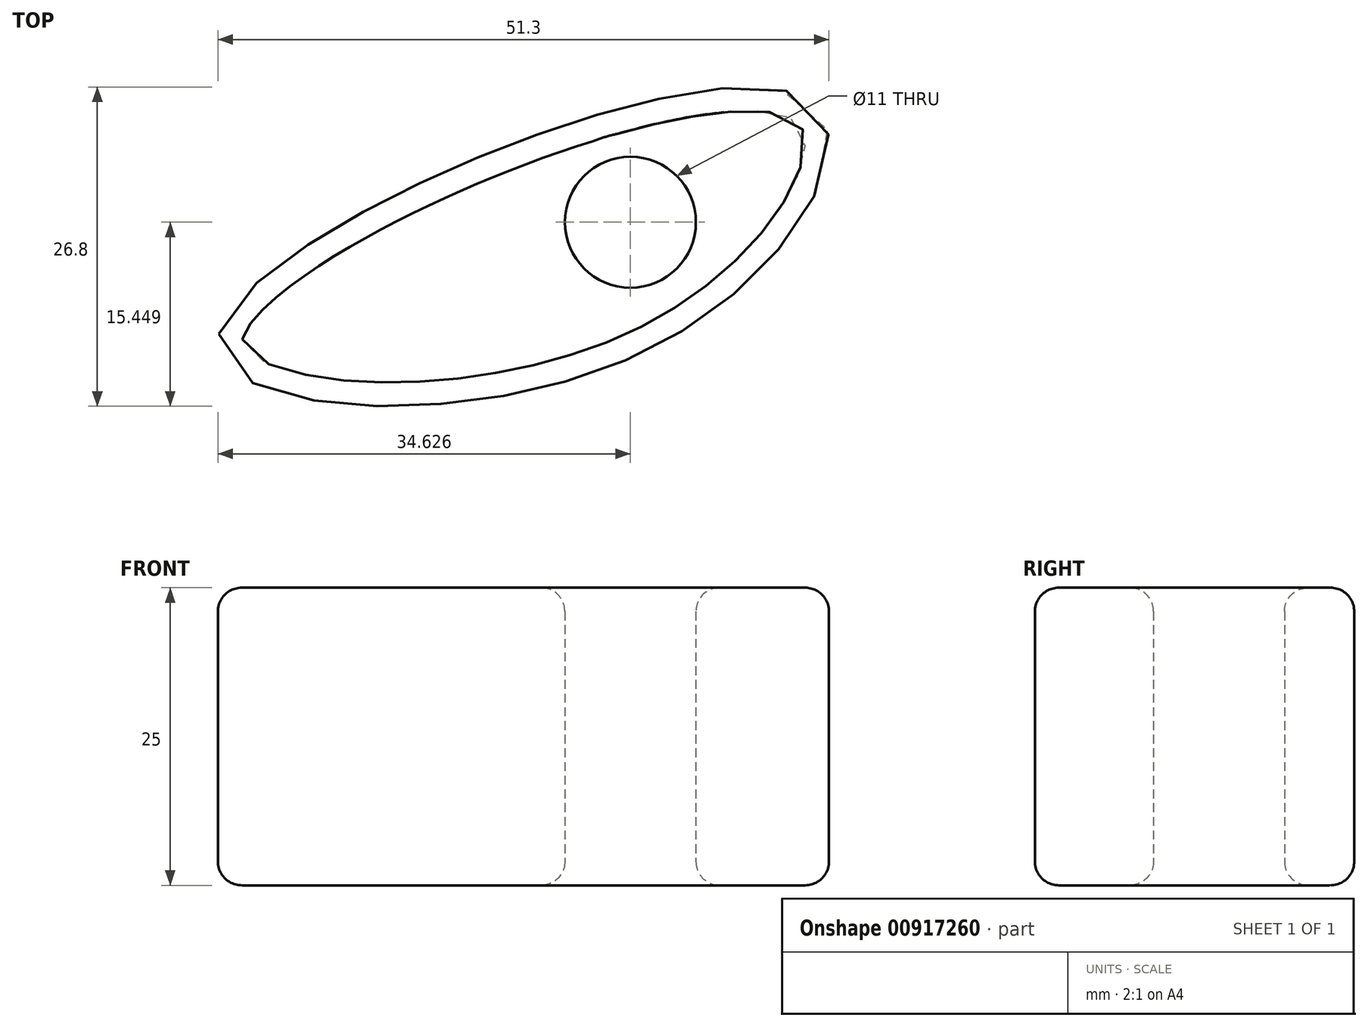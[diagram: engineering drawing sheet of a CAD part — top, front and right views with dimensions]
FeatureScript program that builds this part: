
annotation { "Feature Type Name" : "Feature", "Feature Type Description" : "" }
export const myFeature = defineFeature(function(context is Context, id is Id, definition is map)
    precondition{}
    {
        {
            var Q0;
            Q0=qCreatedBy(makeId("Top.planeOp"),FACE);
            var sketch = newSketch(context, id + "F0", { "sketchPlane" : qUnion([Q0])});
            skFitSpline(sketch, "E0", {"points": [v(-20.03, 0) * mm, v(28.7, 20.05) * mm, v(16.17, -1.26) * mm, v(-20.03, 0) * mm]});
            skCircle(sketch, "E1", {"center": v(14.52, 9.4) * mm, "radius": 5.5 * mm});
            skSolve(sketch);
        }
        {
            var Q0;
            Q0=makeQuery(id+"F0.imprint","IMPRINT",FACE,{"disambiguationData":[TD([[makeQuery(id+"F0.imprint","IMPRINT",EDGE,{"derivedFrom":sQuery(id+"F0.wireOp",EDGE,"E0")}),-1.0]])]});
            extrude(context, id + "F1", {"entities" : qUnion([Q0]), "depth" : 25 * mm, "offsetDistance" : 25 * mm});
        }
        {
            var Q0;
            Q0=makeQuery(id+"F1.opExtrude","SWEPT_FACE",FACE,{"disambiguationData":[OSD([sQuery(id+"F0.wireOp",EDGE,"E0")])]});
            var Q1;
            Q1=makeQuery(id+"F1.opExtrude","SWEPT_FACE",FACE,{"disambiguationData":[OSD([sQuery(id+"F0.wireOp",EDGE,"E1")])]});
            var Q2;
            Q2=makeQuery(id+"F1.opExtrude","CAP_EDGE",EDGE,{"disambiguationData":[OSD([sQuery(id+"F0.wireOp",EDGE,"E0")])],"isStart":false});
            fillet(context, id + "F2", {"entities" : qUnion([Q0, Q1, Q2]), "radius" : 2 * mm, "tangentPropagation" : true, "allowEdgeOverflow" : false});
        }
    });
